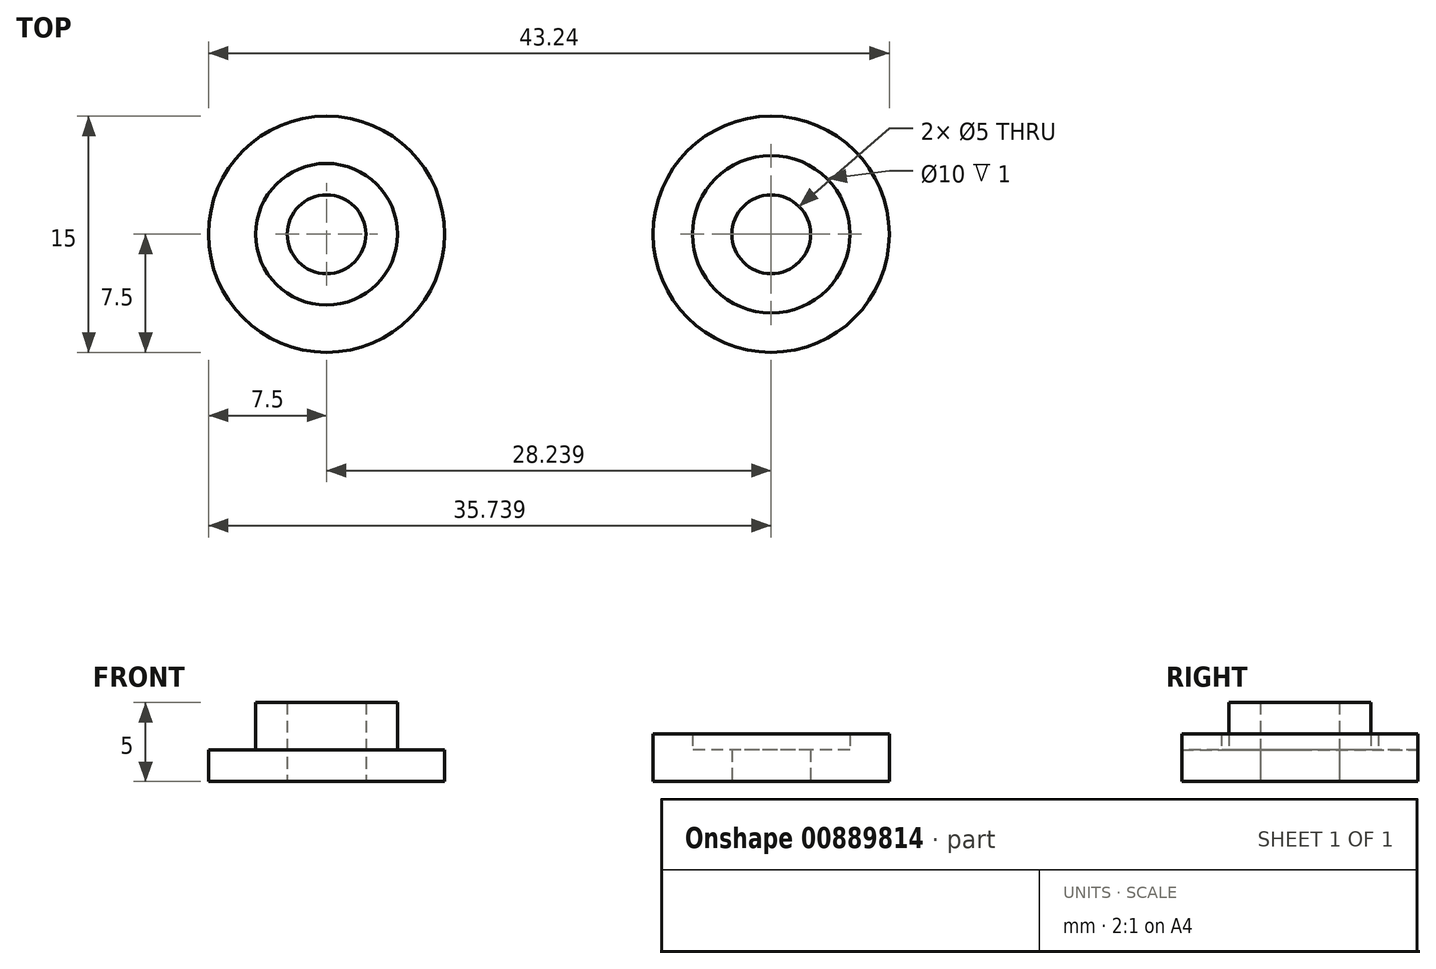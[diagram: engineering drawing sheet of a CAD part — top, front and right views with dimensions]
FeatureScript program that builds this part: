
annotation { "Feature Type Name" : "Feature", "Feature Type Description" : "" }
export const myFeature = defineFeature(function(context is Context, id is Id, definition is map)
    precondition{}
    {
        {
            var Q0;
            Q0=qCreatedBy(makeId("Top.planeOp"),FACE);
            var sketch = newSketch(context, id + "F0", { "sketchPlane" : qUnion([Q0])});
            skCircle(sketch, "E0", {"center": v(0, 0) * mm, "radius": 2.5 * mm});
            skCircle(sketch, "E1", {"center": v(0, 0) * mm, "radius": 4.5 * mm});
            skCircle(sketch, "E2", {"center": v(0, 0) * mm, "radius": 7.5 * mm});
            skCircle(sketch, "E3", {"center": v(28.24, 0) * mm, "radius": 7.5 * mm});
            skCircle(sketch, "E4", {"center": v(28.24, 0) * mm, "radius": 5 * mm});
            skCircle(sketch, "E5", {"center": v(28.24, 0) * mm, "radius": 2.5 * mm});
            skSolve(sketch);
        }
        {
            var Q0;
            Q0=makeQuery(id+"F0.imprint","IMPRINT",FACE,{"disambiguationData":[TD([[makeQuery(id+"F0.imprint","IMPRINT",EDGE,{"derivedFrom":sQuery(id+"F0.wireOp",EDGE,"E4")}),1.0]])]});
            extrude(context, id + "F1", {"entities" : qUnion([Q0]), "depth" : 2 * mm, "offsetDistance" : 25 * mm});
        }
        {
            var Q0;
            Q0=makeQuery(id+"F0.imprint","IMPRINT",FACE,{"disambiguationData":[TD([[makeQuery(id+"F0.imprint","IMPRINT",EDGE,{"derivedFrom":sQuery(id+"F0.wireOp",EDGE,"E3")}),1.0]])]});
            extrude(context, id + "F2", {"entities" : qUnion([Q0]), "operationType" : NewBodyOperationType.ADD, "depth" : 3 * mm, "offsetDistance" : 25 * mm});
        }
        {
            var Q0;
            Q0=makeQuery(id+"F0.imprint","IMPRINT",FACE,{"disambiguationData":[TD([[makeQuery(id+"F0.imprint","IMPRINT",EDGE,{"derivedFrom":sQuery(id+"F0.wireOp",EDGE,"E0")}),-1.0]])]});
            extrude(context, id + "F3", {"entities" : qUnion([Q0]), "depth" : 5 * mm, "offsetDistance" : 25 * mm});
        }
        {
            var Q0;
            Q0=makeQuery(id+"F0.imprint","IMPRINT",FACE,{"disambiguationData":[TD([[makeQuery(id+"F0.imprint","IMPRINT",EDGE,{"derivedFrom":sQuery(id+"F0.wireOp",EDGE,"E1")}),-1.0]])]});
            extrude(context, id + "F4", {"entities" : qUnion([Q0]), "operationType" : NewBodyOperationType.ADD, "depth" : 2 * mm, "offsetDistance" : 25 * mm});
        }
    });
